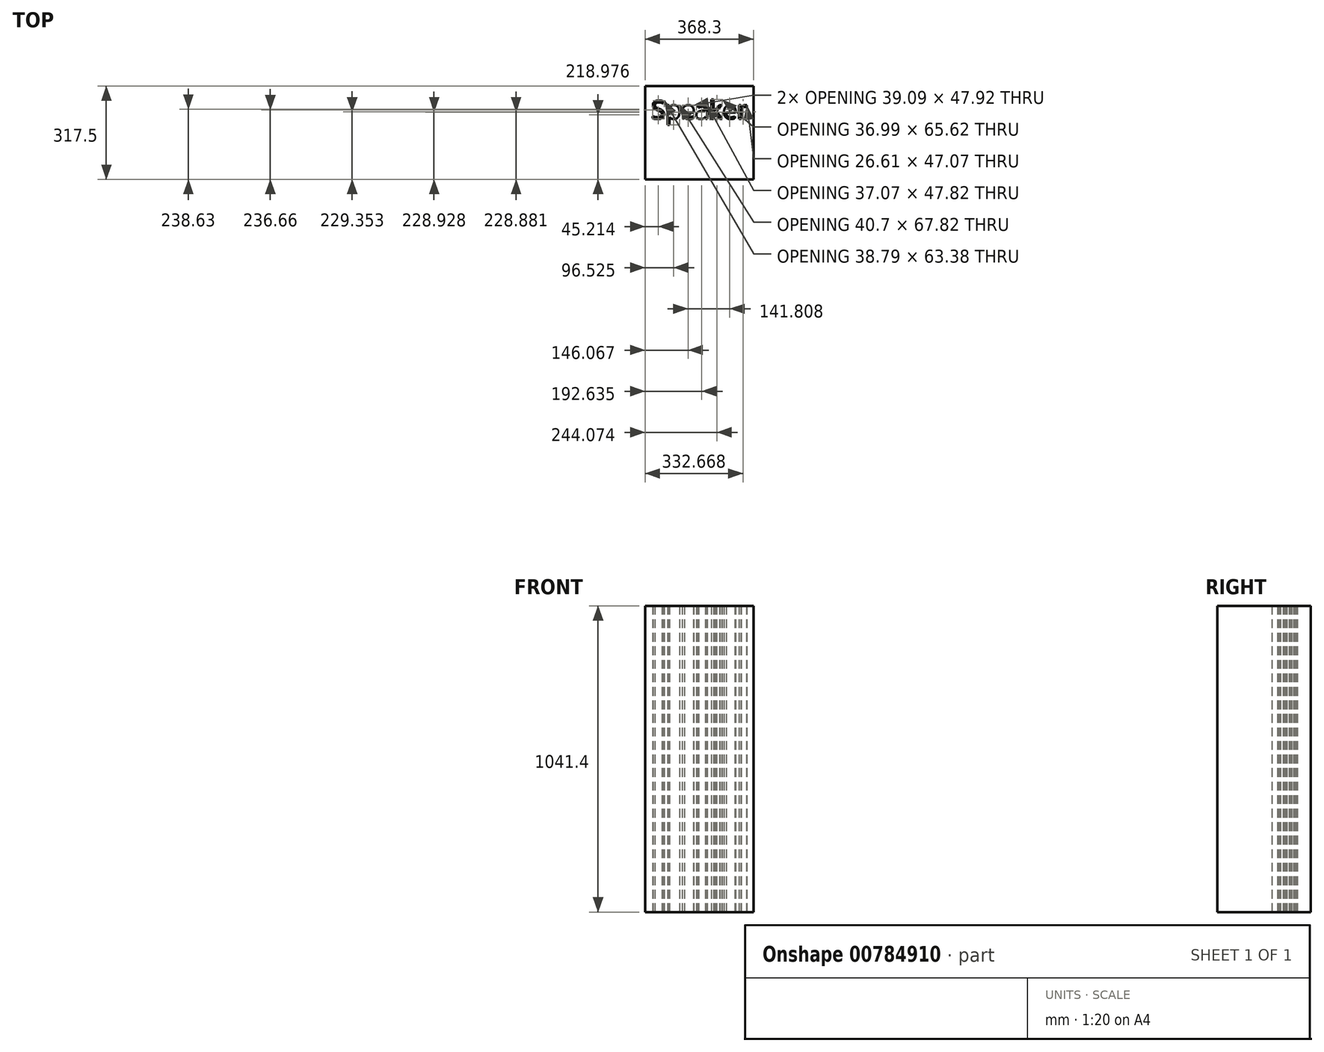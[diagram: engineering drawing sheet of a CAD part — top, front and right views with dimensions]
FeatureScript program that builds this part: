
annotation { "Feature Type Name" : "Feature", "Feature Type Description" : "" }
export const myFeature = defineFeature(function(context is Context, id is Id, definition is map)
    precondition{}
    {
        {
            var Q0;
            Q0=qCreatedBy(makeId("Top.planeOp"),FACE);
            var sketch = newSketch(context, id + "F0", { "sketchPlane" : qUnion([Q0])});
            skLineSegment(sketch, "E0.bottom", {"start": v(184.15, 158.75) * mm, "end": v(-184.15, 158.75) * mm});
            skLineSegment(sketch, "E0.top", {"start": v(184.15, -158.75) * mm, "end": v(-184.15, -158.75) * mm});
            skLineSegment(sketch, "E0.left", {"start": v(184.15, 158.75) * mm, "end": v(184.15, -158.75) * mm});
            skLineSegment(sketch, "E0.right", {"start": v(-184.15, 158.75) * mm, "end": v(-184.15, -158.75) * mm});
            skPoint(sketch, "E0.middle", {"position": v(0, 0) * mm});
            skText(sketch, "E1", { "text": "Speaker", "fontName": "OpenSans-Regular.ttf"});
            const initialGuessF0  = {"E1": [-0.1628, 0.04707, 1, 0, 0.06218]};
            skSetInitialGuess(sketch, initialGuessF0);
            skSolve(sketch);
        }
        {
            var Q0;
            Q0=makeQuery(id+"F0.imprint","IMPRINT",FACE,{"disambiguationData":[TD([[makeQuery(id+"F0.imprint","IMPRINT",EDGE,{"derivedFrom":sQuery(id+"F0.wireOp",EDGE,"E0.bottom")}),1.0]])]});
            extrude(context, id + "F1", {"entities" : qUnion([Q0]), "depth" : 1041.4 * mm, "offsetDistance" : 25.4 * mm});
        }
    });
